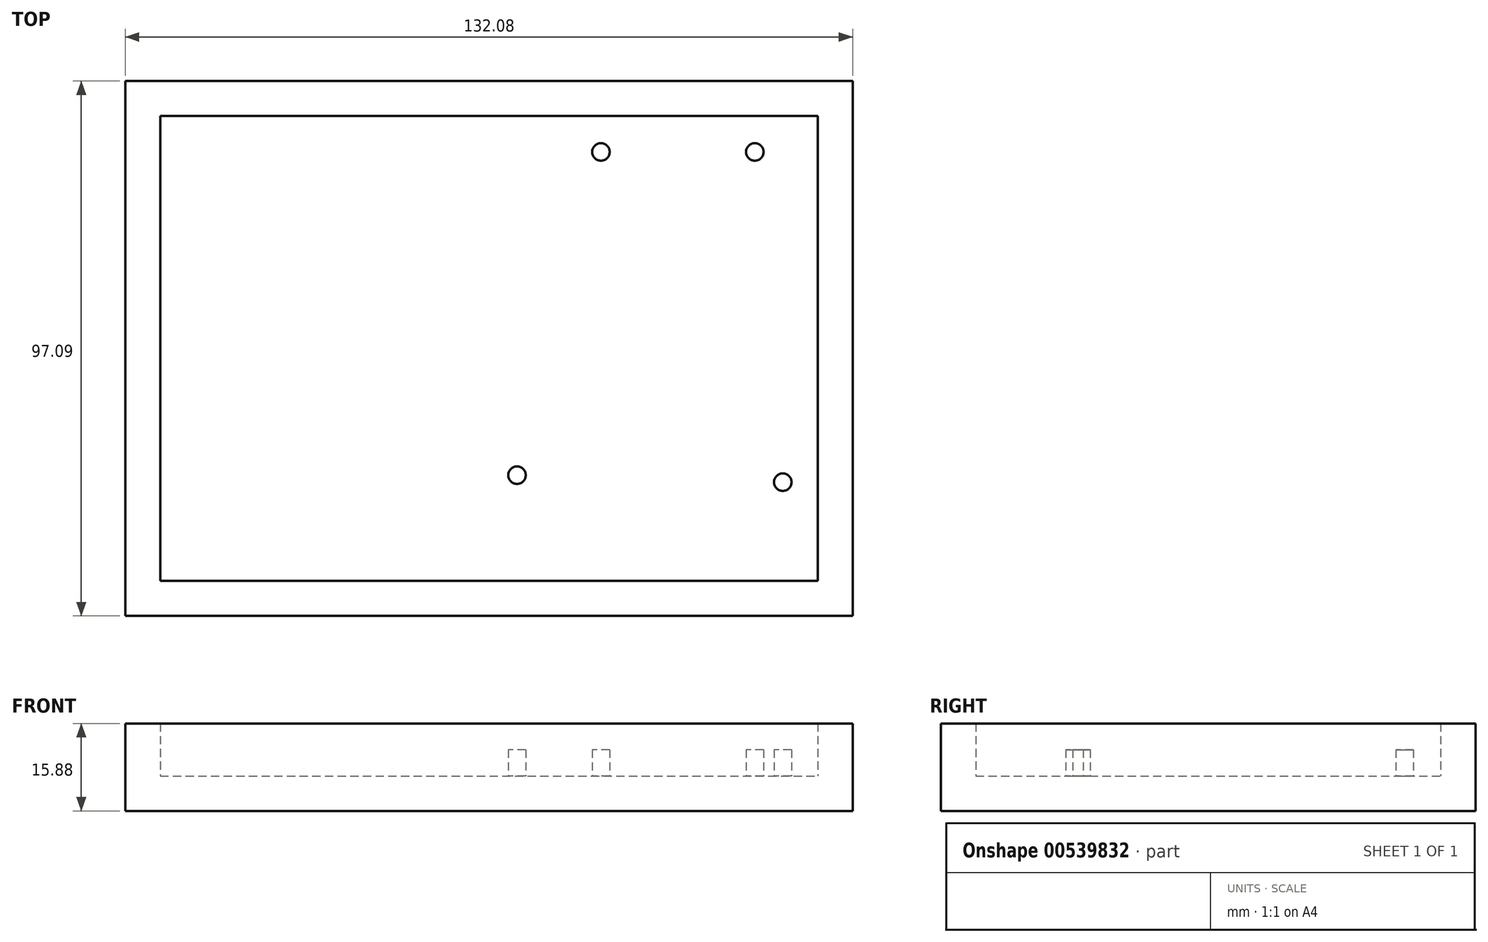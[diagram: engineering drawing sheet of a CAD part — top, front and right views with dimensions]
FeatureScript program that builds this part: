
annotation { "Feature Type Name" : "Feature", "Feature Type Description" : "" }
export const myFeature = defineFeature(function(context is Context, id is Id, definition is map)
    precondition{}
    {
        {
            var Q0;
            Q0=qCreatedBy(makeId("Top.planeOp"),FACE);
            var sketch = newSketch(context, id + "F0", { "sketchPlane" : qUnion([Q0])});
            skLineSegment(sketch, "E0", {"start": v(-54, 94.24) * mm, "end": v(78.08, 94.24) * mm});
            skLineSegment(sketch, "E1", {"start": v(-54, 94.24) * mm, "end": v(-54, -2.85) * mm});
            skLineSegment(sketch, "E2", {"start": v(78.08, 0) * mm, "end": v(78.08, 94.24) * mm});
            skLineSegment(sketch, "E3", {"start": v(78.08, 94.24) * mm, "end": v(78.08, -2.85) * mm});
            skLineSegment(sketch, "E4", {"start": v(78.08, -2.85) * mm, "end": v(-54, -2.85) * mm});
            skLineSegment(sketch, "E5", {"start": v(-54, 94.24) * mm, "end": v(-47.65, 94.24) * mm});
            skLineSegment(sketch, "E6", {"start": v(-47.65, 87.9) * mm, "end": v(-47.65, 3.5) * mm});
            skLineSegment(sketch, "E7", {"start": v(-47.65, 87.9) * mm, "end": v(71.73, 87.9) * mm});
            skLineSegment(sketch, "E8", {"start": v(-47.65, 3.5) * mm, "end": v(71.73, 3.5) * mm});
            skLineSegment(sketch, "E9", {"start": v(71.73, 87.9) * mm, "end": v(71.73, 3.5) * mm});
            skPoint(sketch, "E10.orphan", {"position": v(78.08, 87.9) * mm});
            skPoint(sketch, "E11.orphan", {"position": v(-47.65, -2.85) * mm});
            skLineSegment(sketch, "E12", {"start": v(71.73, 3.5) * mm, "end": v(-47.65, 3.5) * mm});
            skSolve(sketch);
        }
        {
            var Q0;
            Q0=makeQuery(id+"F0.imprint","IMPRINT",FACE,{"disambiguationData":[TD([[makeQuery(id+"F0.imprint","IMPRINT",EDGE,{"derivedFrom":sQuery(id+"F0.wireOp",EDGE,"E6")}),1.0]])]});
            var Q1;
            {var subQ2=sQuery(id+"F0.wireOp",EDGE,"E0");Q1=makeQuery(id+"F0.imprint","IMPRINT",FACE,{"disambiguationData":[TD([[makeQuery(id+"F0.imprint","IMPRINT",EDGE,{"derivedFrom":subQ2}),-1.0]])]});}
            extrude(context, id + "F1", {"entities" : qUnion([Q0, Q1]), "depth" : 6.35 * mm, "offsetDistance" : 25.4 * mm});
        }
        {
            var Q0;
            Q0=makeQuery(id+"F1.opExtrude","CAP_FACE",FACE,{"disambiguationData":[OSD([sQuery(id+"F0.wireOp",EDGE,"E0"),sQuery(id+"F0.wireOp",EDGE,"E1"),sQuery(id+"F0.wireOp",EDGE,"E3"),sQuery(id+"F0.wireOp",EDGE,"E4"),sQuery(id+"F0.wireOp",EDGE,"E5")])],"isStart":false});
            var sketch = newSketch(context, id + "F2", { "sketchPlane" : qUnion([Q0])});
            skLineSegment(sketch, "E13", {"start": v(-54, 94.24) * mm, "end": v(78.08, 94.24) * mm});
            skLineSegment(sketch, "E14", {"start": v(78.08, 94.24) * mm, "end": v(78.08, -2.85) * mm});
            skLineSegment(sketch, "E15", {"start": v(78.08, -2.85) * mm, "end": v(-54, -2.85) * mm});
            skLineSegment(sketch, "E16", {"start": v(-54, -2.85) * mm, "end": v(-54, 94.24) * mm});
            skLineSegment(sketch, "E17", {"start": v(-54, 94.24) * mm, "end": v(-54, 87.9) * mm});
            skLineSegment(sketch, "E18", {"start": v(-47.65, 87.9) * mm, "end": v(71.73, 87.9) * mm});
            skLineSegment(sketch, "E19", {"start": v(78.08, 94.24) * mm, "end": v(71.73, 94.24) * mm});
            skLineSegment(sketch, "E20", {"start": v(71.73, 87.9) * mm, "end": v(71.73, 3.5) * mm});
            skLineSegment(sketch, "E21", {"start": v(78.08, -2.85) * mm, "end": v(78.08, 3.5) * mm});
            skLineSegment(sketch, "E22", {"start": v(71.73, 3.5) * mm, "end": v(-47.65, 3.5) * mm});
            skLineSegment(sketch, "E23", {"start": v(-54, -2.85) * mm, "end": v(-47.65, -2.85) * mm});
            skLineSegment(sketch, "E24", {"start": v(-47.65, 3.5) * mm, "end": v(-47.65, 87.9) * mm});
            skSolve(sketch);
        }
        {
            var Q0;
            Q0=makeQuery(id+"F2.imprint","IMPRINT",FACE,{"disambiguationData":[TD([[makeQuery(id+"F2.imprint","IMPRINT",EDGE,{"derivedFrom":sQuery(id+"F2.wireOp",EDGE,"E13")}),-1.0]])]});
            extrude(context, id + "F3", {"entities" : qUnion([Q0]), "operationType" : NewBodyOperationType.ADD, "depth" : 9.52 * mm, "offsetDistance" : 25.4 * mm});
        }
        {
            var Q0;
            Q0=makeQuery(id+"F1.opExtrude","CAP_FACE",FACE,{"disambiguationData":[OSD([sQuery(id+"F0.wireOp",EDGE,"E0"),sQuery(id+"F0.wireOp",EDGE,"E1"),sQuery(id+"F0.wireOp",EDGE,"E3"),sQuery(id+"F0.wireOp",EDGE,"E4"),sQuery(id+"F0.wireOp",EDGE,"E5")])],"isStart":false});
            var sketch = newSketch(context, id + "F4", { "sketchPlane" : qUnion([Q0])});
            skLineSegment(sketch, "E25", {"start": v(-47.65, 87.9) * mm, "end": v(9.5, 87.9) * mm});
            skLineSegment(sketch, "E26", {"start": v(71.73, 87.9) * mm, "end": v(14.58, 87.9) * mm});
            skLineSegment(sketch, "E27", {"start": v(-47.65, 87.9) * mm, "end": v(-47.65, 3.76) * mm});
            skPoint(sketch, "E28.end.orphan", {"position": v(14.58, 0) * mm});
            skLineSegment(sketch, "E29", {"start": v(14.58, 7.47) * mm, "end": v(21.44, 7.47) * mm});
            skPoint(sketch, "E30.end.orphan", {"position": v(14.58, 3.5) * mm});
            skLineSegment(sketch, "E31", {"start": v(71.73, 7.47) * mm, "end": v(71.73, 83.93) * mm});
            skCircle(sketch, "E32", {"center": v(32.36, 81.39) * mm, "radius": 1.59 * mm});
            skCircle(sketch, "E33", {"center": v(60.3, 81.39) * mm, "radius": 1.59 * mm});
            skCircle(sketch, "E34", {"center": v(17.12, 22.71) * mm, "radius": 1.59 * mm});
            skLineSegment(sketch, "E35", {"start": v(65.38, 19.85) * mm, "end": v(65.38, 21.44) * mm});
            skCircle(sketch, "E36", {"center": v(65.38, 21.44) * mm, "radius": 1.59 * mm});
            skPoint(sketch, "E37.start.orphan", {"position": v(21.44, 7.47) * mm});
            skPoint(sketch, "E38.orphan", {"position": v(21.44, 22.71) * mm});
            skPoint(sketch, "E39.start.orphan", {"position": v(14.58, 22.71) * mm});
            skPoint(sketch, "E40.start.orphan", {"position": v(14.58, 11.7) * mm});
            skPoint(sketch, "E41.end.orphan", {"position": v(65.38, 7.47) * mm});
            skPoint(sketch, "E42.end.orphan", {"position": v(60.3, 83.93) * mm});
            skPoint(sketch, "E43.end.orphan", {"position": v(32.36, 83.93) * mm});
            skPoint(sketch, "E43.start.orphan", {"position": v(14.58, 83.93) * mm});
            skSolve(sketch);
        }
        {
            var Q0;
            Q0 = qSketchRegion(id + "F4", true);
            extrude(context, id + "F5", {"entities" : qUnion([Q0]), "operationType" : NewBodyOperationType.ADD, "depth" : 4.76 * mm, "offsetDistance" : 25.4 * mm});
        }
    });
